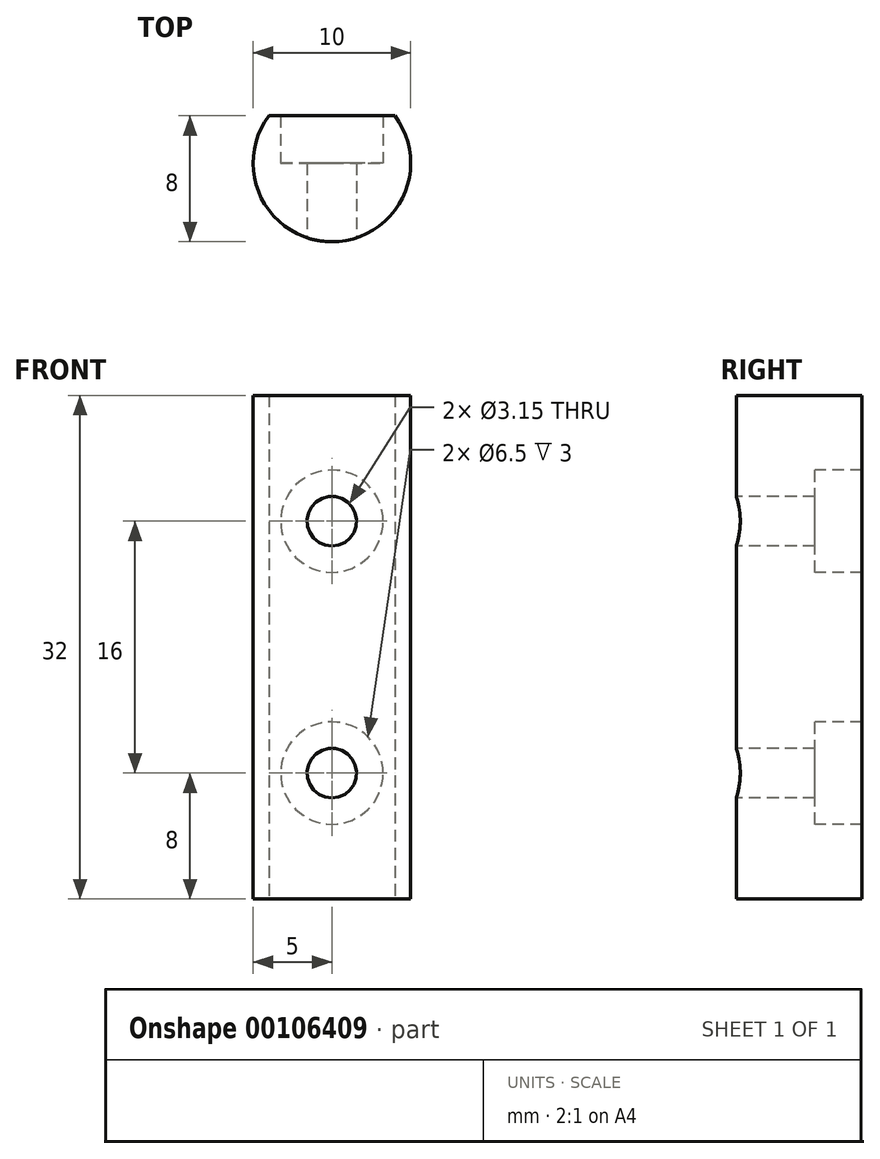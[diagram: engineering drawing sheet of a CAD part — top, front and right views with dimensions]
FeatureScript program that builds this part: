
annotation { "Feature Type Name" : "Feature", "Feature Type Description" : "" }
export const myFeature = defineFeature(function(context is Context, id is Id, definition is map)
    precondition{}
    {
        {
            var Q0;
            Q0=qCreatedBy(makeId("Top.planeOp"),FACE);
            var sketch = newSketch(context, id + "F0", { "sketchPlane" : qUnion([Q0])});
            skLineSegment(sketch, "E0", {"start": v(-4, 3) * mm, "end": v(4, 3) * mm});
            skArc(sketch, "E1", {"start": v(-4, 3) * mm, "mid": v(0, -5) * mm, "end": v(4, 3) * mm});
            skSolve(sketch);
        }
        {
            var Q0;
            Q0=makeQuery(id+"F0.imprint","IMPRINT",FACE,{"disambiguationData":[TD([[makeQuery(id+"F0.imprint","IMPRINT",EDGE,{"derivedFrom":sQuery(id+"F0.wireOp",EDGE,"E0")}),-1.0]])]});
            extrude(context, id + "F1", {"entities" : qUnion([Q0]), "depth" : 32 * mm, "symmetric" : true});
        }
        {
            var Q0;
            Q0=makeQuery(id+"F1.opExtrude","SWEPT_FACE",FACE,{"disambiguationData":[OSD([sQuery(id+"F0.wireOp",EDGE,"E0")])]});
            var sketch = newSketch(context, id + "F2", { "sketchPlane" : qUnion([Q0])});
            skPoint(sketch, "E2", {"position": v(0, 8) * mm});
            skPoint(sketch, "E3", {"position": v(0, -8) * mm});
            skSolve(sketch);
        }
        {
            var Q0;
            Q0=sQuery(id+"F2.wireOp",VERTEX,"E2");
            var Q1;
            Q1=sQuery(id+"F2.wireOp",VERTEX,"E3");
            var Q2;
            Q2=makeQuery(id+"F1.opExtrude","SWEPT_BODY",BODY,{"disambiguationData":[OSD([sQuery(id+"F0.wireOp",EDGE,"E0"),sQuery(id+"F0.wireOp",EDGE,"E1")])]});
            hole(context, id + "F3", {"style" : HoleStyle.C_BORE, "endStyle" : HoleEndStyle.THROUGH, "standardTappedOrClearance" : lookupTablePath({ "standard" : "ISO", "fit" : "Close", "size" : "M3", "type" : "Clearance" }), "standardBlindInLast" : lookupTablePath({ "fit" : "Close", "standard" : "ISO", "size" : "M3", "type" : "Clearance" }), "holeDiameter" : 3.15 * mm, "cBoreDiameter" : 6.5 * mm, "cBoreDepth" : 3 * mm, "locations" : qUnion([Q0, Q1]), "scope" : qUnion([Q2]), "isTappedThrough" : true, "startStyle" : HoleStartStyle.SKETCH});
        }
    });
